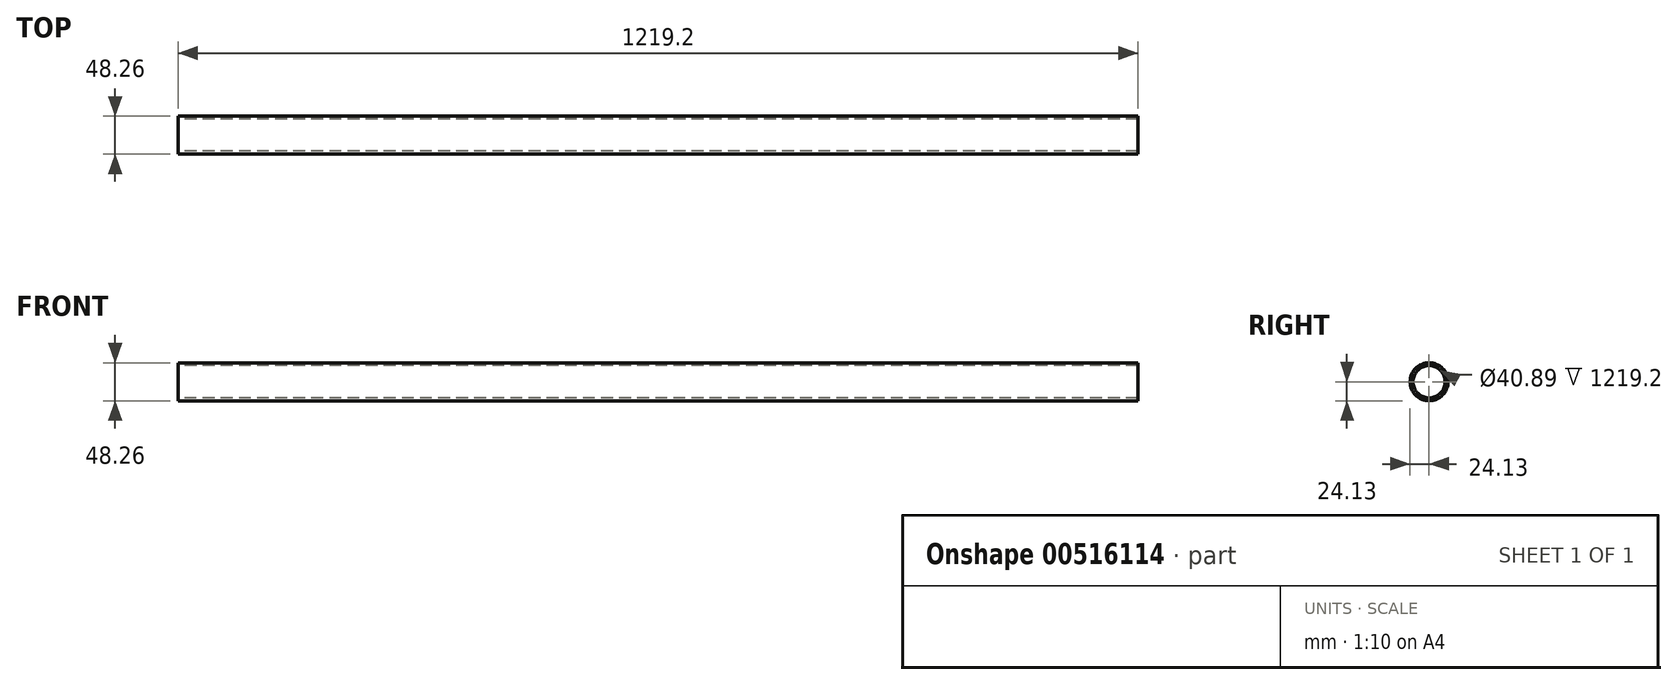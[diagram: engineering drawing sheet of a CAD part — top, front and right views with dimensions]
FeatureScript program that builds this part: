
annotation { "Feature Type Name" : "Feature", "Feature Type Description" : "" }
export const myFeature = defineFeature(function(context is Context, id is Id, definition is map)
    precondition{}
    {
        {
            var Q0;
            Q0=qCreatedBy(makeId("Right.planeOp"),FACE);
            var sketch = newSketch(context, id + "F0", { "sketchPlane" : qUnion([Q0])});
            skCircle(sketch, "E0", {"center": v(0, 0) * mm, "radius": 24.13 * mm});
            skCircle(sketch, "E1", {"center": v(0, 0) * mm, "radius": 20.45 * mm});
            skSolve(sketch);
        }
        {
            var Q0;
            Q0 = qSketchRegion(id + "F0", true);
            extrude(context, id + "F1", {"entities" : qUnion([Q0]), "depth" : 1219.2 * mm, "offsetDistance" : 25.4 * mm});
        }
    });
